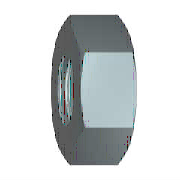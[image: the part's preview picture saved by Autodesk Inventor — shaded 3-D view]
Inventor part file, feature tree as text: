
AUTODESK INVENTOR PART (.ipt)
format: ipt  version: 2019 (Build 230136000, 136)  size: 176,640 bytes
history: native  units: mm (DEFAULTED — no unit token found)
features: sketch x3, chamfer x1, hole x1, other x1, plane x1
ambient origin geometry x7: Origin, YZ Plane, XZ Plane, X Axis, Y Axis, Z Axis, Center Point
bodies: Solid1 (feature_tree), Body (feature_tree)
feature tree (7):
  chamfer  "Chamfer1"  Angle=30.0deg  [1 undecoded]
  hole  "Thread"  [1 undecoded]
  other  "Work Axis1"
  plane  "Work Plane1"
  sketch  "Sketch1"  dims[d0=9.237604mm]
  sketch  "Sketch2"  dims[d1=3.0mm]
  sketch  "Sketch3"  dims[d2=0.0mm d3=30.0deg d4=30.0deg d5=8.0mm d6=8.0mm d7=90.0deg d25=4.134mm d26=6.0mm d27=4.0mm d28=2.0mm d29=14.3117mm d30=8.0mm d31=20.594885mm d8=0.433013mm d9=30.0deg d10=0.433013mm d11=30.0deg d13=0.0mm d14=0.0mm d39=0.0mm d40=0.433013mm d41=0.433013mm d42=0.0mm]
note: 2 required parameter values undecoded (feature->parameter linkage not recoverable at this tier; creation-order binding heuristic only, values carry confidence <= 0.55)
